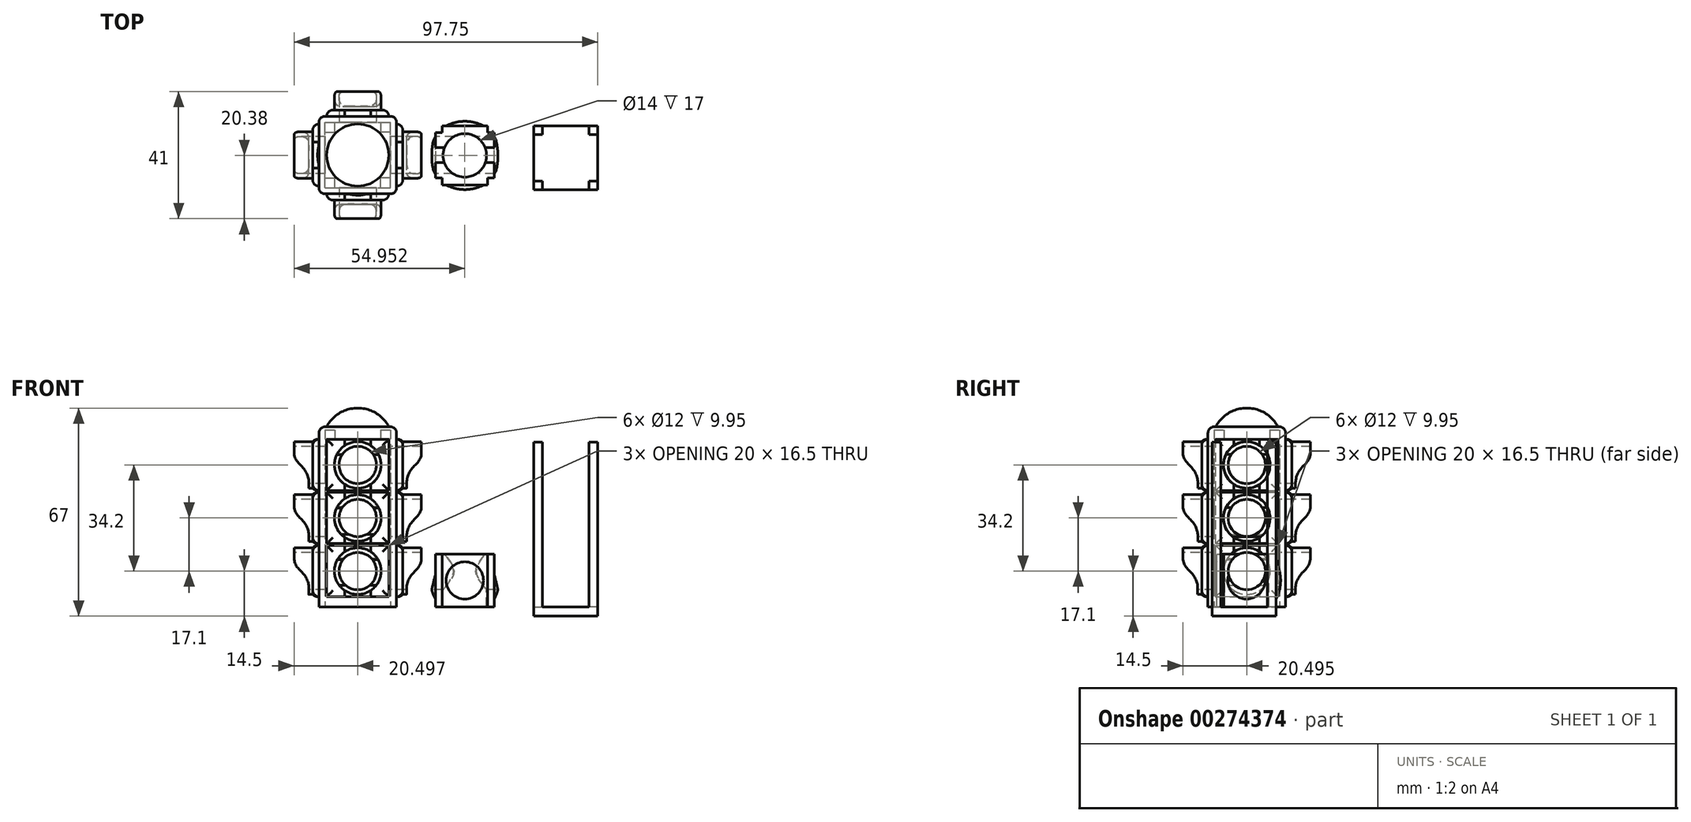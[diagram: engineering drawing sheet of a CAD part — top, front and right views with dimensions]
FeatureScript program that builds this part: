
annotation { "Feature Type Name" : "Feature", "Feature Type Description" : "" }
export const myFeature = defineFeature(function(context is Context, id is Id, definition is map)
    precondition{}
    {
        {
            var Q0;
            Q0=qCreatedBy(makeId("Front.planeOp"),FACE);
            var sketch = newSketch(context, id + "F0", { "sketchPlane" : qUnion([Q0])});
            skLineSegment(sketch, "E0.bottom", {"start": v(-22.57, 17) * mm, "end": v(-3.57, 17) * mm});
            skLineSegment(sketch, "E0.top", {"start": v(-22.57, 0) * mm, "end": v(-3.57, 0) * mm});
            skLineSegment(sketch, "E0.left", {"start": v(-22.57, 17) * mm, "end": v(-22.57, 0) * mm});
            skLineSegment(sketch, "E0.right", {"start": v(-3.57, 17) * mm, "end": v(-3.57, 0) * mm});
            skSolve(sketch);
        }
        {
            var Q0;
            Q0=makeQuery(id+"F0.imprint","IMPRINT",FACE,{"disambiguationData":[TD([[makeQuery(id+"F0.imprint","IMPRINT",EDGE,{"derivedFrom":sQuery(id+"F0.wireOp",EDGE,"E0.bottom")}),-1.0]])]});
            extrude(context, id + "F1", {"entities" : qUnion([Q0]), "depth" : 19 * mm});
        }
        {
            var Q0;
            Q0=makeQuery(id+"F1.opExtrude","CAP_FACE",FACE,{"disambiguationData":[OSD([sQuery(id+"F0.wireOp",EDGE,"E0.bottom"),sQuery(id+"F0.wireOp",EDGE,"E0.top"),sQuery(id+"F0.wireOp",EDGE,"E0.left"),sQuery(id+"F0.wireOp",EDGE,"E0.right")])],"isStart":false});
            var sketch = newSketch(context, id + "F2", { "sketchPlane" : qUnion([Q0])});
            skCircle(sketch, "E1", {"center": v(-13.07, 8.5) * mm, "radius": 6 * mm});
            skPoint(sketch, "E1.centerSnap0", {"position": v(-22.57, 8.5) * mm});
            skSolve(sketch);
        }
        {
            var Q0;
            Q0=makeQuery(id+"F2.imprint","IMPRINT",FACE,{"disambiguationData":[TD([[makeQuery(id+"F2.imprint","IMPRINT",EDGE,{"derivedFrom":sQuery(id+"F2.wireOp",EDGE,"E1")}),1.0]])]});
            extrude(context, id + "F3", {"entities" : qUnion([Q0]), "operationType" : NewBodyOperationType.ADD, "depth" : 1.5 * mm});
        }
        {
            var Q0;
            Q0=makeQuery(id+"F1.opExtrude","SWEPT_FACE",FACE,{"disambiguationData":[OSD([sQuery(id+"F0.wireOp",EDGE,"E0.left")])]});
            var sketch = newSketch(context, id + "F4", { "sketchPlane" : qUnion([Q0])});
            skCircle(sketch, "E2", {"center": v(9.5, 8.5) * mm, "radius": 6 * mm});
            skSolve(sketch);
        }
        {
            var Q0;
            Q0=makeQuery(id+"F4.imprint","IMPRINT",FACE,{"disambiguationData":[TD([[makeQuery(id+"F4.imprint","IMPRINT",EDGE,{"derivedFrom":sQuery(id+"F4.wireOp",EDGE,"E2")}),1.0]])]});
            extrude(context, id + "F5", {"entities" : qUnion([Q0]), "operationType" : NewBodyOperationType.ADD, "depth" : 1.5 * mm});
        }
        {
            var Q0;
            Q0=makeQuery(id+"F1.opExtrude","CAP_FACE",FACE,{"disambiguationData":[OSD([sQuery(id+"F0.wireOp",EDGE,"E0.bottom"),sQuery(id+"F0.wireOp",EDGE,"E0.top"),sQuery(id+"F0.wireOp",EDGE,"E0.left"),sQuery(id+"F0.wireOp",EDGE,"E0.right")])],"isStart":true});
            var sketch = newSketch(context, id + "F6", { "sketchPlane" : qUnion([Q0])});
            skCircle(sketch, "E3", {"center": v(13.07, 8.5) * mm, "radius": 6 * mm});
            skSolve(sketch);
        }
        {
            var Q0;
            Q0=makeQuery(id+"F6.imprint","IMPRINT",FACE,{"disambiguationData":[TD([[makeQuery(id+"F6.imprint","IMPRINT",EDGE,{"derivedFrom":sQuery(id+"F6.wireOp",EDGE,"E3")}),1.0]])]});
            extrude(context, id + "F7", {"entities" : qUnion([Q0]), "operationType" : NewBodyOperationType.ADD, "depth" : 1.5 * mm});
        }
        {
            var Q0;
            Q0=makeQuery(id+"F1.opExtrude","SWEPT_FACE",FACE,{"disambiguationData":[OSD([sQuery(id+"F0.wireOp",EDGE,"E0.right")])]});
            var sketch = newSketch(context, id + "F8", { "sketchPlane" : qUnion([Q0])});
            skCircle(sketch, "E4", {"center": v(-9.5, 8.5) * mm, "radius": 6 * mm});
            skPoint(sketch, "E4.centerSnap0", {"position": v(-19, 8.5) * mm});
            skSolve(sketch);
        }
        {
            var Q0;
            Q0=makeQuery(id+"F8.imprint","IMPRINT",FACE,{"disambiguationData":[TD([[makeQuery(id+"F8.imprint","IMPRINT",EDGE,{"derivedFrom":sQuery(id+"F8.wireOp",EDGE,"E4")}),1.0]])]});
            extrude(context, id + "F9", {"entities" : qUnion([Q0]), "operationType" : NewBodyOperationType.ADD, "depth" : 1.5 * mm});
        }
        {
            var Q0;
            Q0=makeQuery(id+"F3.opExtrude","CAP_EDGE",EDGE,{"disambiguationData":[OSD([sQuery(id+"F2.wireOp",EDGE,"E1")])],"isStart":false});
            var Q1;
            Q1=makeQuery(id+"F5.opExtrude","CAP_EDGE",EDGE,{"disambiguationData":[OSD([sQuery(id+"F4.wireOp",EDGE,"E2")])],"isStart":false});
            var Q2;
            Q2=makeQuery(id+"F7.opExtrude","CAP_EDGE",EDGE,{"disambiguationData":[OSD([sQuery(id+"F6.wireOp",EDGE,"E3")])],"isStart":false});
            var Q3;
            Q3=makeQuery(id+"F9.opExtrude","CAP_EDGE",EDGE,{"disambiguationData":[OSD([sQuery(id+"F8.wireOp",EDGE,"E4")])],"isStart":false});
            fillet(context, id + "F10", {"entities" : qUnion([Q0, Q1, Q2, Q3]), "radius" : 12.7 * mm, "tangentPropagation" : true, "allowEdgeOverflow" : false});
        }
        {
            var Q0;
            Q0=makeQuery(id+"F1.opExtrude","SWEPT_FACE",FACE,{"disambiguationData":[OSD([sQuery(id+"F0.wireOp",EDGE,"E0.bottom")])]});
            var sketch = newSketch(context, id + "F11", { "sketchPlane" : qUnion([Q0])});
            skLineSegment(sketch, "E5.bottom", {"start": v(-22.57, 0) * mm, "end": v(-20.37, 0) * mm});
            skLineSegment(sketch, "E5.top", {"start": v(-22.57, -2.2) * mm, "end": v(-20.37, -2.2) * mm});
            skLineSegment(sketch, "E5.left", {"start": v(-22.57, 0) * mm, "end": v(-22.57, -2.2) * mm});
            skLineSegment(sketch, "E5.right", {"start": v(-20.37, 0) * mm, "end": v(-20.37, -2.2) * mm});
            skLineSegment(sketch, "E6.bottom", {"start": v(-3.57, 0) * mm, "end": v(-5.77, 0) * mm});
            skLineSegment(sketch, "E6.top", {"start": v(-3.57, -2.2) * mm, "end": v(-5.77, -2.2) * mm});
            skLineSegment(sketch, "E6.left", {"start": v(-3.57, 0) * mm, "end": v(-3.57, -2.2) * mm});
            skLineSegment(sketch, "E6.right", {"start": v(-5.77, 0) * mm, "end": v(-5.77, -2.2) * mm});
            skLineSegment(sketch, "E7.bottom", {"start": v(-22.57, -19) * mm, "end": v(-20.37, -19) * mm});
            skLineSegment(sketch, "E7.top", {"start": v(-22.57, -16.8) * mm, "end": v(-20.37, -16.8) * mm});
            skLineSegment(sketch, "E7.left", {"start": v(-22.57, -19) * mm, "end": v(-22.57, -16.8) * mm});
            skLineSegment(sketch, "E7.right", {"start": v(-20.37, -19) * mm, "end": v(-20.37, -16.8) * mm});
            skLineSegment(sketch, "E8.bottom", {"start": v(-3.57, -19) * mm, "end": v(-5.77, -19) * mm});
            skLineSegment(sketch, "E8.top", {"start": v(-3.57, -16.8) * mm, "end": v(-5.77, -16.8) * mm});
            skLineSegment(sketch, "E8.left", {"start": v(-3.57, -19) * mm, "end": v(-3.57, -16.8) * mm});
            skLineSegment(sketch, "E8.right", {"start": v(-5.77, -19) * mm, "end": v(-5.77, -16.8) * mm});
            skSolve(sketch);
        }
        {
            var Q0;
            Q0=makeQuery(id+"F11.imprint","IMPRINT",FACE,{"disambiguationData":[TD([[makeQuery(id+"F11.imprint","IMPRINT",EDGE,{"derivedFrom":sQuery(id+"F11.wireOp",EDGE,"E5.bottom")}),-1.0]])]});
            var Q1;
            Q1=makeQuery(id+"F11.imprint","IMPRINT",FACE,{"disambiguationData":[TD([[makeQuery(id+"F11.imprint","IMPRINT",EDGE,{"derivedFrom":sQuery(id+"F11.wireOp",EDGE,"E6.bottom")}),-1.0]])]});
            var Q2;
            Q2=makeQuery(id+"F11.imprint","IMPRINT",FACE,{"disambiguationData":[TD([[makeQuery(id+"F11.imprint","IMPRINT",EDGE,{"derivedFrom":sQuery(id+"F11.wireOp",EDGE,"E8.bottom")}),1.0]])]});
            var Q3;
            Q3=makeQuery(id+"F11.imprint","IMPRINT",FACE,{"disambiguationData":[TD([[makeQuery(id+"F11.imprint","IMPRINT",EDGE,{"derivedFrom":sQuery(id+"F11.wireOp",EDGE,"E7.bottom")}),1.0]])]});
            extrude(context, id + "F12", {"entities" : qUnion([Q0, Q1, Q2, Q3]), "operationType" : NewBodyOperationType.REMOVE, "endBound" : BoundingType.THROUGH_ALL, "oppositeDirection" : true, "depth" : 25 * mm});
        }
        {
            var Q0;
            Q0=qCreatedBy(makeId("Top.planeOp"),FACE);
            var sketch = newSketch(context, id + "F13", { "sketchPlane" : qUnion([Q0])});
            skLineSegment(sketch, "E9.bottom", {"start": v(9.13, 0) * mm, "end": v(29.73, 0) * mm});
            skLineSegment(sketch, "E9.top", {"start": v(9.13, -20.6) * mm, "end": v(29.73, -20.6) * mm});
            skLineSegment(sketch, "E9.left", {"start": v(9.13, 0) * mm, "end": v(9.13, -20.6) * mm});
            skLineSegment(sketch, "E9.right", {"start": v(29.73, 0) * mm, "end": v(29.73, -20.6) * mm});
            skSolve(sketch);
        }
        {
            var Q0;
            Q0=makeQuery(id+"F13.imprint","IMPRINT",FACE,{"disambiguationData":[TD([[makeQuery(id+"F13.imprint","IMPRINT",EDGE,{"derivedFrom":sQuery(id+"F13.wireOp",EDGE,"E9.bottom")}),-1.0]])]});
            extrude(context, id + "F14", {"entities" : qUnion([Q0]), "oppositeDirection" : true, "depth" : 3 * mm});
        }
        {
            var Q0;
            Q0=makeQuery(id+"F14.opExtrude","CAP_FACE",FACE,{"disambiguationData":[OSD([sQuery(id+"F13.wireOp",EDGE,"E9.bottom"),sQuery(id+"F13.wireOp",EDGE,"E9.top"),sQuery(id+"F13.wireOp",EDGE,"E9.left"),sQuery(id+"F13.wireOp",EDGE,"E9.right")])],"isStart":true});
            var sketch = newSketch(context, id + "F15", { "sketchPlane" : qUnion([Q0])});
            skLineSegment(sketch, "E10.bottom", {"start": v(9.13, 0) * mm, "end": v(11.93, 0) * mm});
            skLineSegment(sketch, "E10.top", {"start": v(9.13, -2.8) * mm, "end": v(11.93, -2.8) * mm});
            skLineSegment(sketch, "E10.left", {"start": v(9.13, 0) * mm, "end": v(9.13, -2.8) * mm});
            skLineSegment(sketch, "E10.right", {"start": v(11.93, 0) * mm, "end": v(11.93, -2.8) * mm});
            skLineSegment(sketch, "E11.bottom", {"start": v(9.13, -20.6) * mm, "end": v(11.93, -20.6) * mm});
            skLineSegment(sketch, "E11.top", {"start": v(9.13, -17.8) * mm, "end": v(11.93, -17.8) * mm});
            skLineSegment(sketch, "E11.left", {"start": v(9.13, -20.6) * mm, "end": v(9.13, -17.8) * mm});
            skLineSegment(sketch, "E11.right", {"start": v(11.93, -20.6) * mm, "end": v(11.93, -17.8) * mm});
            skLineSegment(sketch, "E12.bottom", {"start": v(29.73, 0) * mm, "end": v(26.93, 0) * mm});
            skLineSegment(sketch, "E12.top", {"start": v(29.73, -2.8) * mm, "end": v(26.93, -2.8) * mm});
            skLineSegment(sketch, "E12.left", {"start": v(29.73, 0) * mm, "end": v(29.73, -2.8) * mm});
            skLineSegment(sketch, "E12.right", {"start": v(26.93, 0) * mm, "end": v(26.93, -2.8) * mm});
            skLineSegment(sketch, "E13.bottom", {"start": v(29.73, -20.6) * mm, "end": v(26.93, -20.6) * mm});
            skLineSegment(sketch, "E13.top", {"start": v(29.73, -17.8) * mm, "end": v(26.93, -17.8) * mm});
            skLineSegment(sketch, "E13.left", {"start": v(29.73, -20.6) * mm, "end": v(29.73, -17.8) * mm});
            skLineSegment(sketch, "E13.right", {"start": v(26.93, -20.6) * mm, "end": v(26.93, -17.8) * mm});
            skSolve(sketch);
        }
        {
            var Q0;
            Q0=makeQuery(id+"F15.imprint","IMPRINT",FACE,{"disambiguationData":[TD([[makeQuery(id+"F15.imprint","IMPRINT",EDGE,{"derivedFrom":sQuery(id+"F15.wireOp",EDGE,"E11.bottom")}),1.0]])]});
            var Q1;
            Q1=makeQuery(id+"F15.imprint","IMPRINT",FACE,{"disambiguationData":[TD([[makeQuery(id+"F15.imprint","IMPRINT",EDGE,{"derivedFrom":sQuery(id+"F15.wireOp",EDGE,"E10.bottom")}),-1.0]])]});
            var Q2;
            Q2=makeQuery(id+"F15.imprint","IMPRINT",FACE,{"disambiguationData":[TD([[makeQuery(id+"F15.imprint","IMPRINT",EDGE,{"derivedFrom":sQuery(id+"F15.wireOp",EDGE,"E12.bottom")}),-1.0]])]});
            var Q3;
            Q3=makeQuery(id+"F15.imprint","IMPRINT",FACE,{"disambiguationData":[TD([[makeQuery(id+"F15.imprint","IMPRINT",EDGE,{"derivedFrom":sQuery(id+"F15.wireOp",EDGE,"E13.bottom")}),1.0]])]});
            extrude(context, id + "F16", {"entities" : qUnion([Q0, Q1, Q2, Q3]), "operationType" : NewBodyOperationType.ADD, "depth" : 53 * mm});
        }
        {
            var Q0;
            Q0=qCreatedBy(makeId("Top.planeOp"),FACE);
            var sketch = newSketch(context, id + "F17", { "sketchPlane" : qUnion([Q0])});
            skLineSegment(sketch, "E14.bottom", {"start": v(-60.02, 3.12) * mm, "end": v(-35.02, 3.12) * mm});
            skLineSegment(sketch, "E14.top", {"start": v(-60.02, -21.88) * mm, "end": v(-35.02, -21.88) * mm});
            skLineSegment(sketch, "E14.left", {"start": v(-60.02, 3.12) * mm, "end": v(-60.02, -21.88) * mm});
            skLineSegment(sketch, "E14.right", {"start": v(-35.02, 3.12) * mm, "end": v(-35.02, -21.88) * mm});
            skSolve(sketch);
        }
        {
            var Q0;
            Q0=makeQuery(id+"F17.imprint","IMPRINT",FACE,{"disambiguationData":[TD([[makeQuery(id+"F17.imprint","IMPRINT",EDGE,{"derivedFrom":sQuery(id+"F17.wireOp",EDGE,"E14.bottom")}),-1.0]])]});
            extrude(context, id + "F18", {"entities" : qUnion([Q0]), "depth" : 58 * mm});
        }
        {
            var Q0;
            Q0=makeQuery(id+"F18.opExtrude","CAP_FACE",FACE,{"disambiguationData":[OSD([sQuery(id+"F17.wireOp",EDGE,"E14.bottom"),sQuery(id+"F17.wireOp",EDGE,"E14.top"),sQuery(id+"F17.wireOp",EDGE,"E14.left"),sQuery(id+"F17.wireOp",EDGE,"E14.right")])],"isStart":true});
            var sketch = newSketch(context, id + "F19", { "sketchPlane" : qUnion([Q0])});
            skLineSegment(sketch, "E15.bottom", {"start": v(-58.07, 19.93) * mm, "end": v(-36.97, 19.93) * mm});
            skLineSegment(sketch, "E15.top", {"start": v(-58.07, -1.17) * mm, "end": v(-36.97, -1.17) * mm});
            skLineSegment(sketch, "E15.left", {"start": v(-58.07, 19.93) * mm, "end": v(-58.07, -1.17) * mm});
            skLineSegment(sketch, "E15.right", {"start": v(-36.97, 19.93) * mm, "end": v(-36.97, -1.17) * mm});
            skPoint(sketch, "E15.middle", {"position": v(-47.52, 9.38) * mm});
            skSolve(sketch);
        }
        {
            var Q0;
            Q0=makeQuery(id+"F18.opExtrude","SWEPT_FACE",FACE,{"disambiguationData":[OSD([sQuery(id+"F17.wireOp",EDGE,"E14.top")])]});
            var sketch = newSketch(context, id + "F20", { "sketchPlane" : qUnion([Q0])});
            skCircle(sketch, "E16", {"center": v(-47.52, 11.5) * mm, "radius": 6 * mm});
            skCircle(sketch, "E17.0.1.0", {"center": v(-47.52, 28.6) * mm, "radius": 6 * mm});
            skCircle(sketch, "E17.0.2.0", {"center": v(-47.52, 45.7) * mm, "radius": 6 * mm});
            skLineSegment(sketch, "E17.direction1", {"start": v(-47.52, 11.5) * mm, "end": v(-22.52, 11.5) * mm, "construction": true});
            skLineSegment(sketch, "E17.direction2", {"start": v(-47.52, 11.5) * mm, "end": v(-47.52, 28.6) * mm, "construction": true});
            skCircle(sketch, "E18", {"center": v(-47.52, 11.5) * mm, "radius": 7.5 * mm});
            skCircle(sketch, "E19.0.1.0", {"center": v(-47.52, 28.6) * mm, "radius": 7.5 * mm});
            skCircle(sketch, "E19.0.2.0", {"center": v(-47.52, 45.7) * mm, "radius": 7.5 * mm});
            skLineSegment(sketch, "E20.bottom", {"start": v(-37.52, 19.75) * mm, "end": v(-57.52, 19.75) * mm});
            skLineSegment(sketch, "E20.top", {"start": v(-37.52, 3.25) * mm, "end": v(-57.52, 3.25) * mm});
            skLineSegment(sketch, "E20.left", {"start": v(-37.52, 19.75) * mm, "end": v(-37.52, 3.25) * mm});
            skLineSegment(sketch, "E20.right", {"start": v(-57.52, 19.75) * mm, "end": v(-57.52, 3.25) * mm});
            skLineSegment(sketch, "E21.0.1.0", {"start": v(-37.52, 36.85) * mm, "end": v(-57.52, 36.85) * mm});
            skLineSegment(sketch, "E21.0.1.1", {"start": v(-37.52, 36.85) * mm, "end": v(-37.52, 20.35) * mm});
            skLineSegment(sketch, "E21.0.1.2", {"start": v(-37.52, 20.35) * mm, "end": v(-57.52, 20.35) * mm});
            skLineSegment(sketch, "E21.0.1.3", {"start": v(-57.52, 36.85) * mm, "end": v(-57.52, 20.35) * mm});
            skLineSegment(sketch, "E21.0.2.0", {"start": v(-37.52, 53.95) * mm, "end": v(-57.52, 53.95) * mm});
            skLineSegment(sketch, "E21.0.2.1", {"start": v(-37.52, 53.95) * mm, "end": v(-37.52, 37.45) * mm});
            skLineSegment(sketch, "E21.0.2.2", {"start": v(-37.52, 37.45) * mm, "end": v(-57.52, 37.45) * mm});
            skLineSegment(sketch, "E21.0.2.3", {"start": v(-57.52, 53.95) * mm, "end": v(-57.52, 37.45) * mm});
            skLineSegment(sketch, "E21.direction1", {"start": v(-57.52, 3.25) * mm, "end": v(-32.52, 3.25) * mm, "construction": true});
            skLineSegment(sketch, "E21.direction2", {"start": v(-57.52, 3.25) * mm, "end": v(-57.52, 20.35) * mm, "construction": true});
            skSolve(sketch);
        }
        {
            var Q0;
            Q0=makeQuery(id+"F20.imprint","IMPRINT",FACE,{"disambiguationData":[TD([[makeQuery(id+"F20.imprint","IMPRINT",EDGE,{"derivedFrom":sQuery(id+"F20.wireOp",EDGE,"E16")}),1.0]])]});
            var Q1;
            Q1=makeQuery(id+"F20.imprint","IMPRINT",FACE,{"disambiguationData":[TD([[makeQuery(id+"F20.imprint","IMPRINT",EDGE,{"derivedFrom":sQuery(id+"F20.wireOp",EDGE,"E17.0.1.0")}),1.0]])]});
            var Q2;
            Q2=makeQuery(id+"F20.imprint","IMPRINT",FACE,{"disambiguationData":[TD([[makeQuery(id+"F20.imprint","IMPRINT",EDGE,{"derivedFrom":sQuery(id+"F20.wireOp",EDGE,"E17.0.2.0")}),1.0]])]});
            extrude(context, id + "F21", {"entities" : qUnion([Q0, Q1, Q2]), "operationType" : NewBodyOperationType.REMOVE, "flatOperationType" : FlatOperationType.REMOVE, "endBound" : BoundingType.THROUGH_ALL, "oppositeDirection" : true, "offsetDistance" : 25 * mm, "depth" : 25 * mm, "domain" : OperationDomain.MODEL});
        }
        {
            var Q0;
            Q0=makeQuery(id+"F20.imprint","IMPRINT",FACE,{"disambiguationData":[TD([[makeQuery(id+"F20.imprint","IMPRINT",EDGE,{"derivedFrom":sQuery(id+"F20.wireOp",EDGE,"E17.0.2.0")}),-1.0]])]});
            var Q1;
            Q1=makeQuery(id+"F20.imprint","IMPRINT",FACE,{"disambiguationData":[TD([[makeQuery(id+"F20.imprint","IMPRINT",EDGE,{"derivedFrom":sQuery(id+"F20.wireOp",EDGE,"E17.0.1.0")}),-1.0]])]});
            var Q2;
            Q2=makeQuery(id+"F20.imprint","IMPRINT",FACE,{"disambiguationData":[TD([[makeQuery(id+"F20.imprint","IMPRINT",EDGE,{"derivedFrom":sQuery(id+"F20.wireOp",EDGE,"E16")}),-1.0]])]});
            extrude(context, id + "F22", {"entities" : qUnion([Q0, Q1, Q2]), "operationType" : NewBodyOperationType.ADD, "flatOperationType" : FlatOperationType.REMOVE, "offsetDistance" : 25 * mm, "depth" : 8 * mm, "hasSecondDirection" : true, "secondDirectionOppositeDirection" : true, "secondDirectionDepth" : 33 * mm, "domain" : OperationDomain.MODEL});
        }
        {
            var Q0;
            Q0=makeQuery(id+"F20.imprint","IMPRINT",FACE,{"disambiguationData":[TD([[makeQuery(id+"F20.imprint","IMPRINT",EDGE,{"derivedFrom":sQuery(id+"F20.wireOp",EDGE,"E19.0.2.0")}),-1.0]])]});
            var Q1;
            Q1=makeQuery(id+"F20.imprint","IMPRINT",FACE,{"disambiguationData":[TD([[makeQuery(id+"F20.imprint","IMPRINT",EDGE,{"derivedFrom":sQuery(id+"F20.wireOp",EDGE,"E19.0.1.0")}),-1.0]])]});
            var Q2;
            Q2=makeQuery(id+"F20.imprint","IMPRINT",FACE,{"disambiguationData":[TD([[makeQuery(id+"F20.imprint","IMPRINT",EDGE,{"derivedFrom":sQuery(id+"F20.wireOp",EDGE,"E18")}),-1.0]])]});
            extrude(context, id + "F23", {"entities" : qUnion([Q0, Q1, Q2]), "operationType" : NewBodyOperationType.ADD, "flatOperationType" : FlatOperationType.REMOVE, "offsetDistance" : 25 * mm, "depth" : 2 * mm, "hasSecondDirection" : true, "secondDirectionOppositeDirection" : true, "secondDirectionDepth" : 27 * mm, "domain" : OperationDomain.MODEL});
        }
        {
            var Q0;
            Q0=makeQuery(id+"F18.opExtrude","SWEPT_FACE",FACE,{"disambiguationData":[OSD([sQuery(id+"F17.wireOp",EDGE,"E14.left")])]});
            var sketch = newSketch(context, id + "F24", { "sketchPlane" : qUnion([Q0])});
            skCircle(sketch, "E22", {"center": v(9.38, 11.5) * mm, "radius": 6 * mm});
            skCircle(sketch, "E23.0.1.0", {"center": v(9.38, 28.6) * mm, "radius": 6 * mm});
            skCircle(sketch, "E23.0.2.0", {"center": v(9.38, 45.7) * mm, "radius": 6 * mm});
            skLineSegment(sketch, "E23.direction1", {"start": v(9.38, 11.5) * mm, "end": v(34.38, 11.5) * mm, "construction": true});
            skLineSegment(sketch, "E23.direction2", {"start": v(9.38, 11.5) * mm, "end": v(9.38, 28.6) * mm, "construction": true});
            skCircle(sketch, "E24", {"center": v(9.38, 11.5) * mm, "radius": 7.5 * mm});
            skCircle(sketch, "E25.0.1.0", {"center": v(9.38, 28.6) * mm, "radius": 7.5 * mm});
            skCircle(sketch, "E25.0.2.0", {"center": v(9.38, 45.7) * mm, "radius": 7.5 * mm});
            skLineSegment(sketch, "E26.bottom", {"start": v(19.38, 3.25) * mm, "end": v(-0.62, 3.25) * mm});
            skLineSegment(sketch, "E26.top", {"start": v(19.38, 19.75) * mm, "end": v(-0.62, 19.75) * mm});
            skLineSegment(sketch, "E26.left", {"start": v(19.38, 3.25) * mm, "end": v(19.38, 19.75) * mm});
            skLineSegment(sketch, "E26.right", {"start": v(-0.62, 3.25) * mm, "end": v(-0.62, 19.75) * mm});
            skLineSegment(sketch, "E27.0.1.0", {"start": v(19.38, 36.85) * mm, "end": v(-0.62, 36.85) * mm});
            skLineSegment(sketch, "E27.0.1.1", {"start": v(19.38, 20.35) * mm, "end": v(19.38, 36.85) * mm});
            skLineSegment(sketch, "E27.0.1.2", {"start": v(19.38, 20.35) * mm, "end": v(-0.62, 20.35) * mm});
            skLineSegment(sketch, "E27.0.1.3", {"start": v(-0.62, 20.35) * mm, "end": v(-0.62, 36.85) * mm});
            skLineSegment(sketch, "E27.0.2.0", {"start": v(19.38, 53.95) * mm, "end": v(-0.62, 53.95) * mm});
            skLineSegment(sketch, "E27.0.2.1", {"start": v(19.38, 37.45) * mm, "end": v(19.38, 53.95) * mm});
            skLineSegment(sketch, "E27.0.2.2", {"start": v(19.38, 37.45) * mm, "end": v(-0.62, 37.45) * mm});
            skLineSegment(sketch, "E27.0.2.3", {"start": v(-0.62, 37.45) * mm, "end": v(-0.62, 53.95) * mm});
            skLineSegment(sketch, "E27.direction1", {"start": v(-0.62, 3.25) * mm, "end": v(24.38, 3.25) * mm, "construction": true});
            skLineSegment(sketch, "E27.direction2", {"start": v(-0.62, 3.25) * mm, "end": v(-0.62, 20.35) * mm, "construction": true});
            skSolve(sketch);
        }
        {
            var Q0;
            Q0=makeQuery(id+"F24.imprint","IMPRINT",FACE,{"disambiguationData":[TD([[makeQuery(id+"F24.imprint","IMPRINT",EDGE,{"derivedFrom":sQuery(id+"F24.wireOp",EDGE,"E23.0.2.0")}),1.0]])]});
            var Q1;
            Q1=makeQuery(id+"F24.imprint","IMPRINT",FACE,{"disambiguationData":[TD([[makeQuery(id+"F24.imprint","IMPRINT",EDGE,{"derivedFrom":sQuery(id+"F24.wireOp",EDGE,"E23.0.1.0")}),1.0]])]});
            var Q2;
            Q2=makeQuery(id+"F24.imprint","IMPRINT",FACE,{"disambiguationData":[TD([[makeQuery(id+"F24.imprint","IMPRINT",EDGE,{"derivedFrom":sQuery(id+"F24.wireOp",EDGE,"E22")}),1.0]])]});
            extrude(context, id + "F25", {"entities" : qUnion([Q0, Q1, Q2]), "operationType" : NewBodyOperationType.REMOVE, "endBound" : BoundingType.THROUGH_ALL, "oppositeDirection" : true, "depth" : 25 * mm});
        }
        {
            var Q0;
            Q0=makeQuery(id+"F24.imprint","IMPRINT",FACE,{"disambiguationData":[TD([[makeQuery(id+"F24.imprint","IMPRINT",EDGE,{"derivedFrom":sQuery(id+"F24.wireOp",EDGE,"E22")}),-1.0]])]});
            var Q1;
            Q1=makeQuery(id+"F24.imprint","IMPRINT",FACE,{"disambiguationData":[TD([[makeQuery(id+"F24.imprint","IMPRINT",EDGE,{"derivedFrom":sQuery(id+"F24.wireOp",EDGE,"E23.0.1.0")}),-1.0]])]});
            var Q2;
            Q2=makeQuery(id+"F24.imprint","IMPRINT",FACE,{"disambiguationData":[TD([[makeQuery(id+"F24.imprint","IMPRINT",EDGE,{"derivedFrom":sQuery(id+"F24.wireOp",EDGE,"E23.0.2.0")}),-1.0]])]});
            extrude(context, id + "F26", {"entities" : qUnion([Q0, Q1, Q2]), "operationType" : NewBodyOperationType.ADD, "depth" : 8 * mm, "hasSecondDirection" : true, "secondDirectionOppositeDirection" : true, "secondDirectionDepth" : 33 * mm});
        }
        {
            var Q0;
            Q0=makeQuery(id+"F24.imprint","IMPRINT",FACE,{"disambiguationData":[TD([[makeQuery(id+"F24.imprint","IMPRINT",EDGE,{"derivedFrom":sQuery(id+"F24.wireOp",EDGE,"E24")}),-1.0]])]});
            var Q1;
            Q1=makeQuery(id+"F24.imprint","IMPRINT",FACE,{"disambiguationData":[TD([[makeQuery(id+"F24.imprint","IMPRINT",EDGE,{"derivedFrom":sQuery(id+"F24.wireOp",EDGE,"E25.0.1.0")}),-1.0]])]});
            var Q2;
            Q2=makeQuery(id+"F24.imprint","IMPRINT",FACE,{"disambiguationData":[TD([[makeQuery(id+"F24.imprint","IMPRINT",EDGE,{"derivedFrom":sQuery(id+"F24.wireOp",EDGE,"E25.0.2.0")}),-1.0]])]});
            extrude(context, id + "F27", {"entities" : qUnion([Q0, Q1, Q2]), "operationType" : NewBodyOperationType.ADD, "depth" : 2 * mm, "hasSecondDirection" : true, "secondDirectionOppositeDirection" : true, "secondDirectionDepth" : 27 * mm});
        }
        {
            var Q0;
            Q0=makeQuery(id+"F19.imprint","IMPRINT",FACE,{"disambiguationData":[TD([[makeQuery(id+"F19.imprint","IMPRINT",EDGE,{"derivedFrom":sQuery(id+"F19.wireOp",EDGE,"E15.bottom")}),-1.0]])]});
            extrude(context, id + "F28", {"entities" : qUnion([Q0]), "operationType" : NewBodyOperationType.REMOVE, "oppositeDirection" : true, "depth" : 54 * mm});
        }
        {
            var Q0;
            Q0=makeQuery(id+"F28.boolean.opBoolean","COPY",FACE,{"derivedFrom":makeQuery(id+"F28.opExtrude","CAP_FACE",FACE,{"disambiguationData":[OSD([sQuery(id+"F19.wireOp",EDGE,"E15.bottom"),sQuery(id+"F19.wireOp",EDGE,"E15.top"),sQuery(id+"F19.wireOp",EDGE,"E15.left"),sQuery(id+"F19.wireOp",EDGE,"E15.right")])],"isStart":false})});
            var sketch = newSketch(context, id + "F29", { "sketchPlane" : qUnion([Q0])});
            skLineSegment(sketch, "E28.bottom", {"start": v(-58.07, 19.93) * mm, "end": v(-54.87, 19.93) * mm});
            skLineSegment(sketch, "E28.top", {"start": v(-58.07, 16.73) * mm, "end": v(-54.87, 16.73) * mm});
            skLineSegment(sketch, "E28.left", {"start": v(-58.07, 19.93) * mm, "end": v(-58.07, 16.73) * mm});
            skLineSegment(sketch, "E28.right", {"start": v(-54.87, 19.93) * mm, "end": v(-54.87, 16.73) * mm});
            skLineSegment(sketch, "E29.bottom", {"start": v(-58.07, 2.03) * mm, "end": v(-54.87, 2.03) * mm});
            skLineSegment(sketch, "E29.top", {"start": v(-58.07, -1.17) * mm, "end": v(-54.87, -1.17) * mm});
            skLineSegment(sketch, "E29.left", {"start": v(-58.07, 2.03) * mm, "end": v(-58.07, -1.17) * mm});
            skLineSegment(sketch, "E29.right", {"start": v(-54.87, 2.03) * mm, "end": v(-54.87, -1.17) * mm});
            skLineSegment(sketch, "E30.bottom", {"start": v(-36.97, -1.17) * mm, "end": v(-40.17, -1.17) * mm});
            skLineSegment(sketch, "E30.top", {"start": v(-36.97, 2.03) * mm, "end": v(-40.17, 2.03) * mm});
            skLineSegment(sketch, "E30.left", {"start": v(-36.97, -1.17) * mm, "end": v(-36.97, 2.03) * mm});
            skLineSegment(sketch, "E30.right", {"start": v(-40.17, -1.17) * mm, "end": v(-40.17, 2.03) * mm});
            skLineSegment(sketch, "E31.bottom", {"start": v(-36.97, 19.93) * mm, "end": v(-40.17, 19.93) * mm});
            skLineSegment(sketch, "E31.top", {"start": v(-36.97, 16.73) * mm, "end": v(-40.17, 16.73) * mm});
            skLineSegment(sketch, "E31.left", {"start": v(-36.97, 19.93) * mm, "end": v(-36.97, 16.73) * mm});
            skLineSegment(sketch, "E31.right", {"start": v(-40.17, 19.93) * mm, "end": v(-40.17, 16.73) * mm});
            skSolve(sketch);
        }
        {
            var Q0;
            Q0=makeQuery(id+"F29.imprint","IMPRINT",FACE,{"disambiguationData":[TD([[makeQuery(id+"F29.imprint","IMPRINT",EDGE,{"derivedFrom":sQuery(id+"F29.wireOp",EDGE,"E28.bottom")}),-1.0]])]});
            var Q1;
            Q1=makeQuery(id+"F29.imprint","IMPRINT",FACE,{"disambiguationData":[TD([[makeQuery(id+"F29.imprint","IMPRINT",EDGE,{"derivedFrom":sQuery(id+"F29.wireOp",EDGE,"E31.bottom")}),-1.0]])]});
            var Q2;
            Q2=makeQuery(id+"F29.imprint","IMPRINT",FACE,{"disambiguationData":[TD([[makeQuery(id+"F29.imprint","IMPRINT",EDGE,{"derivedFrom":sQuery(id+"F29.wireOp",EDGE,"E30.bottom")}),1.0]])]});
            var Q3;
            Q3=makeQuery(id+"F29.imprint","IMPRINT",FACE,{"disambiguationData":[TD([[makeQuery(id+"F29.imprint","IMPRINT",EDGE,{"derivedFrom":sQuery(id+"F29.wireOp",EDGE,"E29.bottom")}),-1.0]])]});
            extrude(context, id + "F30", {"entities" : qUnion([Q0, Q1, Q2, Q3]), "operationType" : NewBodyOperationType.REMOVE, "oppositeDirection" : true, "depth" : 3 * mm});
        }
        {
            var Q0;
            Q0=makeQuery(id+"F18.opExtrude","CAP_FACE",FACE,{"disambiguationData":[OSD([sQuery(id+"F17.wireOp",EDGE,"E14.bottom"),sQuery(id+"F17.wireOp",EDGE,"E14.top"),sQuery(id+"F17.wireOp",EDGE,"E14.left"),sQuery(id+"F17.wireOp",EDGE,"E14.right")])],"isStart":false});
            var sketch = newSketch(context, id + "F31", { "sketchPlane" : qUnion([Q0])});
            skCircle(sketch, "E32", {"center": v(-47.52, -9.38) * mm, "radius": 10 * mm});
            skPoint(sketch, "E32.centerSnap0", {"position": v(-47.52, -19.82) * mm});
            skSolve(sketch);
        }
        {
            var Q0;
            Q0=makeQuery(id+"F31.imprint","IMPRINT",FACE,{"disambiguationData":[TD([[makeQuery(id+"F31.imprint","IMPRINT",EDGE,{"derivedFrom":sQuery(id+"F31.wireOp",EDGE,"E32")}),1.0]])]});
            extrude(context, id + "F32", {"entities" : qUnion([Q0]), "operationType" : NewBodyOperationType.ADD, "depth" : 6 * mm});
        }
        {
            var Q0;
            Q0=makeQuery(id+"F23.opExtrude","CAP_EDGE",EDGE,{"disambiguationData":[OSD([sQuery(id+"F20.wireOp",EDGE,"E21.0.2.0")])],"isStart":false});
            var Q1;
            Q1=makeQuery(id+"F23.opExtrude","CAP_EDGE",EDGE,{"disambiguationData":[OSD([sQuery(id+"F20.wireOp",EDGE,"E21.0.2.1")])],"isStart":false});
            var Q2;
            Q2=makeQuery(id+"F23.opExtrude","CAP_EDGE",EDGE,{"disambiguationData":[OSD([sQuery(id+"F20.wireOp",EDGE,"E21.0.2.2")])],"isStart":false});
            var Q3;
            Q3=makeQuery(id+"F23.opExtrude","CAP_EDGE",EDGE,{"disambiguationData":[OSD([sQuery(id+"F20.wireOp",EDGE,"E21.0.2.3")])],"isStart":false});
            var Q4;
            Q4=makeQuery(id+"F23.opExtrude","CAP_EDGE",EDGE,{"disambiguationData":[OSD([sQuery(id+"F20.wireOp",EDGE,"E21.0.1.3")])],"isStart":false});
            var Q5;
            Q5=makeQuery(id+"F23.opExtrude","CAP_EDGE",EDGE,{"disambiguationData":[OSD([sQuery(id+"F20.wireOp",EDGE,"E21.0.1.2")])],"isStart":false});
            var Q6;
            Q6=makeQuery(id+"F23.opExtrude","CAP_EDGE",EDGE,{"disambiguationData":[OSD([sQuery(id+"F20.wireOp",EDGE,"E21.0.1.1")])],"isStart":false});
            var Q7;
            Q7=makeQuery(id+"F23.opExtrude","CAP_EDGE",EDGE,{"disambiguationData":[OSD([sQuery(id+"F20.wireOp",EDGE,"E21.0.1.0")])],"isStart":false});
            var Q8;
            Q8=makeQuery(id+"F23.opExtrude","CAP_EDGE",EDGE,{"disambiguationData":[OSD([sQuery(id+"F20.wireOp",EDGE,"E20.bottom")])],"isStart":false});
            var Q9;
            Q9=makeQuery(id+"F23.opExtrude","CAP_EDGE",EDGE,{"disambiguationData":[OSD([sQuery(id+"F20.wireOp",EDGE,"E20.left")])],"isStart":false});
            var Q10;
            Q10=makeQuery(id+"F23.opExtrude","CAP_EDGE",EDGE,{"disambiguationData":[OSD([sQuery(id+"F20.wireOp",EDGE,"E20.top")])],"isStart":false});
            var Q11;
            Q11=makeQuery(id+"F23.opExtrude","CAP_EDGE",EDGE,{"disambiguationData":[OSD([sQuery(id+"F20.wireOp",EDGE,"E20.right")])],"isStart":false});
            var Q12;
            Q12=makeQuery(id+"F23.opExtrude","CAP_EDGE",EDGE,{"disambiguationData":[OSD([sQuery(id+"F20.wireOp",EDGE,"E21.0.2.0")])],"isStart":true});
            var Q13;
            Q13=makeQuery(id+"F23.opExtrude","CAP_EDGE",EDGE,{"disambiguationData":[OSD([sQuery(id+"F20.wireOp",EDGE,"E21.0.2.3")])],"isStart":true});
            var Q14;
            Q14=makeQuery(id+"F23.opExtrude","CAP_EDGE",EDGE,{"disambiguationData":[OSD([sQuery(id+"F20.wireOp",EDGE,"E21.0.2.1")])],"isStart":true});
            var Q15;
            Q15=makeQuery(id+"F23.opExtrude","CAP_EDGE",EDGE,{"disambiguationData":[OSD([sQuery(id+"F20.wireOp",EDGE,"E21.0.2.2")])],"isStart":true});
            var Q16;
            Q16=makeQuery(id+"F23.opExtrude","CAP_EDGE",EDGE,{"disambiguationData":[OSD([sQuery(id+"F20.wireOp",EDGE,"E21.0.1.0")])],"isStart":true});
            var Q17;
            Q17=makeQuery(id+"F23.opExtrude","CAP_EDGE",EDGE,{"disambiguationData":[OSD([sQuery(id+"F20.wireOp",EDGE,"E21.0.1.1")])],"isStart":true});
            var Q18;
            Q18=makeQuery(id+"F23.opExtrude","CAP_EDGE",EDGE,{"disambiguationData":[OSD([sQuery(id+"F20.wireOp",EDGE,"E21.0.1.3")])],"isStart":true});
            var Q19;
            Q19=makeQuery(id+"F23.opExtrude","CAP_EDGE",EDGE,{"disambiguationData":[OSD([sQuery(id+"F20.wireOp",EDGE,"E21.0.1.2")])],"isStart":true});
            var Q20;
            Q20=makeQuery(id+"F23.opExtrude","CAP_EDGE",EDGE,{"disambiguationData":[OSD([sQuery(id+"F20.wireOp",EDGE,"E20.left")])],"isStart":true});
            var Q21;
            Q21=makeQuery(id+"F23.opExtrude","CAP_EDGE",EDGE,{"disambiguationData":[OSD([sQuery(id+"F20.wireOp",EDGE,"E20.bottom")])],"isStart":true});
            var Q22;
            Q22=makeQuery(id+"F23.opExtrude","CAP_EDGE",EDGE,{"disambiguationData":[OSD([sQuery(id+"F20.wireOp",EDGE,"E20.right")])],"isStart":true});
            var Q23;
            Q23=makeQuery(id+"F23.opExtrude","CAP_EDGE",EDGE,{"disambiguationData":[OSD([sQuery(id+"F20.wireOp",EDGE,"E20.top")])],"isStart":true});
            var Q24;
            Q24=makeQuery(id+"F18.opExtrude","SWEPT_EDGE",EDGE,{"disambiguationData":[OSD([sQuery(id+"F17.wireOp",EDGE,"E14.bottom"),sQuery(id+"F17.wireOp",EDGE,"E14.left")])]});
            var Q25;
            Q25=makeQuery(id+"F18.opExtrude","CAP_EDGE",EDGE,{"disambiguationData":[OSD([sQuery(id+"F17.wireOp",EDGE,"E14.left")])],"isStart":false});
            var Q26;
            Q26=makeQuery(id+"F18.opExtrude","CAP_EDGE",EDGE,{"disambiguationData":[OSD([sQuery(id+"F17.wireOp",EDGE,"E14.bottom")])],"isStart":false});
            var Q27;
            Q27=makeQuery(id+"F18.opExtrude","CAP_EDGE",EDGE,{"disambiguationData":[OSD([sQuery(id+"F17.wireOp",EDGE,"E14.right")])],"isStart":false});
            var Q28;
            Q28=makeQuery(id+"F18.opExtrude","CAP_EDGE",EDGE,{"disambiguationData":[OSD([sQuery(id+"F17.wireOp",EDGE,"E14.top")])],"isStart":false});
            var Q29;
            Q29=makeQuery(id+"F18.opExtrude","SWEPT_EDGE",EDGE,{"disambiguationData":[OSD([sQuery(id+"F17.wireOp",EDGE,"E14.top"),sQuery(id+"F17.wireOp",EDGE,"E14.left")])]});
            var Q30;
            Q30=makeQuery(id+"F18.opExtrude","SWEPT_EDGE",EDGE,{"disambiguationData":[OSD([sQuery(id+"F17.wireOp",EDGE,"E14.top"),sQuery(id+"F17.wireOp",EDGE,"E14.right")])]});
            var Q31;
            Q31=makeQuery(id+"F18.opExtrude","SWEPT_EDGE",EDGE,{"disambiguationData":[OSD([sQuery(id+"F17.wireOp",EDGE,"E14.bottom"),sQuery(id+"F17.wireOp",EDGE,"E14.right")])]});
            var Q32;
            Q32=makeQuery(id+"F27.opExtrude","CAP_EDGE",EDGE,{"disambiguationData":[OSD([sQuery(id+"F24.wireOp",EDGE,"E27.0.2.0")])],"isStart":false});
            var Q33;
            Q33=makeQuery(id+"F27.opExtrude","CAP_EDGE",EDGE,{"disambiguationData":[OSD([sQuery(id+"F24.wireOp",EDGE,"E27.0.2.1")])],"isStart":false});
            var Q34;
            Q34=makeQuery(id+"F27.opExtrude","CAP_EDGE",EDGE,{"disambiguationData":[OSD([sQuery(id+"F24.wireOp",EDGE,"E27.0.2.2")])],"isStart":false});
            var Q35;
            Q35=makeQuery(id+"F27.opExtrude","CAP_EDGE",EDGE,{"disambiguationData":[OSD([sQuery(id+"F24.wireOp",EDGE,"E27.0.2.3")])],"isStart":false});
            var Q36;
            Q36=makeQuery(id+"F27.opExtrude","CAP_EDGE",EDGE,{"disambiguationData":[OSD([sQuery(id+"F24.wireOp",EDGE,"E27.0.1.3")])],"isStart":false});
            var Q37;
            Q37=makeQuery(id+"F27.opExtrude","CAP_EDGE",EDGE,{"disambiguationData":[OSD([sQuery(id+"F24.wireOp",EDGE,"E27.0.1.0")])],"isStart":false});
            var Q38;
            Q38=makeQuery(id+"F27.opExtrude","CAP_EDGE",EDGE,{"disambiguationData":[OSD([sQuery(id+"F24.wireOp",EDGE,"E27.0.1.1")])],"isStart":false});
            var Q39;
            Q39=makeQuery(id+"F27.opExtrude","CAP_EDGE",EDGE,{"disambiguationData":[OSD([sQuery(id+"F24.wireOp",EDGE,"E27.0.1.2")])],"isStart":false});
            var Q40;
            Q40=makeQuery(id+"F27.opExtrude","CAP_EDGE",EDGE,{"disambiguationData":[OSD([sQuery(id+"F24.wireOp",EDGE,"E26.top")])],"isStart":false});
            var Q41;
            Q41=makeQuery(id+"F27.opExtrude","CAP_EDGE",EDGE,{"disambiguationData":[OSD([sQuery(id+"F24.wireOp",EDGE,"E26.right")])],"isStart":false});
            var Q42;
            Q42=makeQuery(id+"F27.opExtrude","CAP_EDGE",EDGE,{"disambiguationData":[OSD([sQuery(id+"F24.wireOp",EDGE,"E26.bottom")])],"isStart":false});
            var Q43;
            Q43=makeQuery(id+"F27.opExtrude","CAP_EDGE",EDGE,{"disambiguationData":[OSD([sQuery(id+"F24.wireOp",EDGE,"E26.left")])],"isStart":false});
            var Q44;
            Q44=makeQuery(id+"F27.opExtrude","CAP_EDGE",EDGE,{"disambiguationData":[OSD([sQuery(id+"F24.wireOp",EDGE,"E26.bottom")])],"isStart":true});
            var Q45;
            Q45=makeQuery(id+"F27.opExtrude","CAP_EDGE",EDGE,{"disambiguationData":[OSD([sQuery(id+"F24.wireOp",EDGE,"E26.left")])],"isStart":true});
            var Q46;
            Q46=makeQuery(id+"F27.opExtrude","CAP_EDGE",EDGE,{"disambiguationData":[OSD([sQuery(id+"F24.wireOp",EDGE,"E26.top")])],"isStart":true});
            var Q47;
            Q47=makeQuery(id+"F27.opExtrude","CAP_EDGE",EDGE,{"disambiguationData":[OSD([sQuery(id+"F24.wireOp",EDGE,"E26.right")])],"isStart":true});
            var Q48;
            Q48=makeQuery(id+"F27.opExtrude","CAP_EDGE",EDGE,{"disambiguationData":[OSD([sQuery(id+"F24.wireOp",EDGE,"E27.0.1.2")])],"isStart":true});
            var Q49;
            Q49=makeQuery(id+"F27.opExtrude","CAP_EDGE",EDGE,{"disambiguationData":[OSD([sQuery(id+"F24.wireOp",EDGE,"E27.0.1.1")])],"isStart":true});
            var Q50;
            Q50=makeQuery(id+"F27.opExtrude","CAP_EDGE",EDGE,{"disambiguationData":[OSD([sQuery(id+"F24.wireOp",EDGE,"E27.0.1.0")])],"isStart":true});
            var Q51;
            Q51=makeQuery(id+"F27.opExtrude","CAP_EDGE",EDGE,{"disambiguationData":[OSD([sQuery(id+"F24.wireOp",EDGE,"E27.0.1.3")])],"isStart":true});
            var Q52;
            Q52=makeQuery(id+"F27.opExtrude","CAP_EDGE",EDGE,{"disambiguationData":[OSD([sQuery(id+"F24.wireOp",EDGE,"E27.0.2.0")])],"isStart":true});
            var Q53;
            Q53=makeQuery(id+"F27.opExtrude","CAP_EDGE",EDGE,{"disambiguationData":[OSD([sQuery(id+"F24.wireOp",EDGE,"E27.0.2.1")])],"isStart":true});
            var Q54;
            Q54=makeQuery(id+"F27.opExtrude","CAP_EDGE",EDGE,{"disambiguationData":[OSD([sQuery(id+"F24.wireOp",EDGE,"E27.0.2.2")])],"isStart":true});
            var Q55;
            Q55=makeQuery(id+"F27.opExtrude","CAP_EDGE",EDGE,{"disambiguationData":[OSD([sQuery(id+"F24.wireOp",EDGE,"E27.0.2.3")])],"isStart":true});
            fillet(context, id + "F33", {"entities" : qUnion([Q0, Q1, Q2, Q3, Q4, Q5, Q6, Q7, Q8, Q9, Q10, Q11, Q12, Q13, Q14, Q15, Q16, Q17, Q18, Q19, Q20, Q21, Q22, Q23, Q24, Q25, Q26, Q27, Q28, Q29, Q30, Q31, Q32, Q33, Q34, Q35, Q36, Q37, Q38, Q39, Q40, Q41, Q42, Q43, Q44, Q45, Q46, Q47, Q48, Q49, Q50, Q51, Q52, Q53, Q54, Q55]), "radius" : 2 * mm, "tangentPropagation" : true, "allowEdgeOverflow" : false});
        }
        {
            var Q0;
            Q0=makeQuery(id+"F32.opExtrude","CAP_EDGE",EDGE,{"disambiguationData":[OSD([sQuery(id+"F31.wireOp",EDGE,"E32")])],"isStart":false});
            fillet(context, id + "F34", {"entities" : qUnion([Q0]), "radius" : 11.1 * mm, "tangentPropagation" : true, "allowEdgeOverflow" : false});
        }
        {
            var Q0;
            Q0=qCreatedBy(makeId("Front.planeOp"),FACE);
            var sketch = newSketch(context, id + "F35", { "sketchPlane" : qUnion([Q0])});
            skLineSegment(sketch, "E33.bottom", {"start": v(-26.89, 51.46) * mm, "end": v(-31.77, 51.46) * mm});
            skLineSegment(sketch, "E33.top", {"start": v(-26.89, 38.04) * mm, "end": v(-31.77, 38.04) * mm});
            skLineSegment(sketch, "E33.left", {"start": v(-26.89, 51.46) * mm, "end": v(-26.89, 38.04) * mm});
            skLineSegment(sketch, "E33.right", {"start": v(-31.77, 51.46) * mm, "end": v(-31.77, 38.04) * mm});
            skFitSpline(sketch, "E34", {"points": [v(-26.89, 50.72) * mm, v(-29.48, 45.2) * mm, v(-31.77, 39.8) * mm], "startDerivative": vector(0, -20.02) * mm, "endDerivative": vector(0, -14.5) * mm});
            skLineSegment(sketch, "E35.bottom", {"start": v(-26.9, 34.25) * mm, "end": v(-31.8, 34.25) * mm});
            skLineSegment(sketch, "E35.top", {"start": v(-26.9, 20.84) * mm, "end": v(-31.8, 20.84) * mm});
            skLineSegment(sketch, "E35.left", {"start": v(-26.9, 34.25) * mm, "end": v(-26.9, 20.84) * mm});
            skLineSegment(sketch, "E35.right", {"start": v(-31.8, 34.25) * mm, "end": v(-31.8, 20.84) * mm});
            skFitSpline(sketch, "E36", {"points": [v(-26.9, 33.5) * mm, v(-29.5, 28) * mm, v(-31.8, 22.6) * mm], "startDerivative": vector(0, -20.02) * mm, "endDerivative": vector(0, -14.5) * mm});
            skLineSegment(sketch, "E37.bottom", {"start": v(-26.94, 17.35) * mm, "end": v(-31.82, 17.35) * mm});
            skLineSegment(sketch, "E37.top", {"start": v(-26.94, 3.93) * mm, "end": v(-31.82, 3.93) * mm});
            skLineSegment(sketch, "E37.left", {"start": v(-26.94, 17.35) * mm, "end": v(-26.94, 3.93) * mm});
            skLineSegment(sketch, "E37.right", {"start": v(-31.82, 17.35) * mm, "end": v(-31.82, 3.93) * mm});
            skFitSpline(sketch, "E38", {"points": [v(-26.94, 16.6) * mm, v(-29.53, 11.1) * mm, v(-31.82, 5.7) * mm], "startDerivative": vector(0, -20.02) * mm, "endDerivative": vector(0, -14.5) * mm});
            skLineSegment(sketch, "E39.right", {"start": v(-63.23, 51.51) * mm, "end": v(-63.23, 38.1) * mm});
            skLineSegment(sketch, "E40.right", {"start": v(-63.25, 34.3) * mm, "end": v(-63.25, 20.88) * mm});
            skLineSegment(sketch, "E41.right", {"start": v(-63.28, 17.4) * mm, "end": v(-63.28, 3.98) * mm});
            skFitSpline(sketch, "E42.MirrorCS", {"points": [v(-68.1, 33.56) * mm, v(-65.5, 28.04) * mm, v(-63.22, 22.65) * mm], "startDerivative": vector(0, -20.02) * mm, "endDerivative": vector(0, -14.5) * mm});
            skFitSpline(sketch, "E43.MirrorCS", {"points": [v(-68.12, 50.76) * mm, v(-65.52, 45.25) * mm, v(-63.23, 39.86) * mm], "startDerivative": vector(0, -20.02) * mm, "endDerivative": vector(0, -14.5) * mm});
            skFitSpline(sketch, "E44.MirrorCS", {"points": [v(-68.07, 16.65) * mm, v(-65.48, 11.14) * mm, v(-63.18, 5.74) * mm], "startDerivative": vector(0, -20.02) * mm, "endDerivative": vector(0, -14.5) * mm});
            skLineSegment(sketch, "E45.MirrorCS", {"start": v(-68.1, 34.3) * mm, "end": v(-68.1, 20.88) * mm});
            skLineSegment(sketch, "E46.MirrorCS", {"start": v(-68.12, 51.51) * mm, "end": v(-68.12, 38.1) * mm});
            skLineSegment(sketch, "E47.MirrorCS", {"start": v(-68.07, 17.4) * mm, "end": v(-63.18, 17.4) * mm});
            skLineSegment(sketch, "E48.MirrorCS", {"start": v(-63.22, 34.3) * mm, "end": v(-63.22, 20.88) * mm});
            skLineSegment(sketch, "E49.MirrorCS", {"start": v(-68.1, 20.88) * mm, "end": v(-63.22, 20.88) * mm});
            skLineSegment(sketch, "E50.MirrorCS", {"start": v(-63.18, 17.4) * mm, "end": v(-63.18, 3.98) * mm});
            skLineSegment(sketch, "E51.MirrorCS", {"start": v(-68.12, 51.51) * mm, "end": v(-63.23, 51.51) * mm});
            skLineSegment(sketch, "E52.MirrorCS", {"start": v(-68.07, 17.4) * mm, "end": v(-68.07, 3.98) * mm});
            skLineSegment(sketch, "E53.MirrorCS", {"start": v(-68.1, 34.3) * mm, "end": v(-63.22, 34.3) * mm});
            skLineSegment(sketch, "E54.MirrorCS", {"start": v(-68.12, 38.1) * mm, "end": v(-63.23, 38.1) * mm});
            skLineSegment(sketch, "E55.MirrorCS", {"start": v(-68.07, 3.98) * mm, "end": v(-63.18, 3.98) * mm});
            skSolve(sketch);
        }
        {
            var Q0;
            {var subQ2=sQuery(id+"F35.wireOp",EDGE,"E33.top");Q0=makeQuery(id+"F35.imprint","IMPRINT",FACE,{"disambiguationData":[TD([[makeQuery(id+"F35.imprint","IMPRINT",EDGE,{"derivedFrom":subQ2}),-1.0]])]});}
            var Q1;
            {var subQ0=sQuery(id+"F35.wireOp",EDGE,"E35.top");Q1=makeQuery(id+"F35.imprint","IMPRINT",FACE,{"disambiguationData":[TD([[makeQuery(id+"F35.imprint","IMPRINT",EDGE,{"derivedFrom":subQ0}),-1.0]])]});}
            var Q2;
            {var subQ0=sQuery(id+"F35.wireOp",EDGE,"E37.top");Q2=makeQuery(id+"F35.imprint","IMPRINT",FACE,{"disambiguationData":[TD([[makeQuery(id+"F35.imprint","IMPRINT",EDGE,{"derivedFrom":subQ0}),-1.0]])]});}
            var Q3;
            {var subQ2=sQuery(id+"F35.wireOp",EDGE,"E43.MirrorCS");Q3=makeQuery(id+"F35.imprint","IMPRINT",FACE,{"disambiguationData":[TD([[makeQuery(id+"F35.imprint","IMPRINT",EDGE,{"derivedFrom":subQ2}),-1.0]])]});}
            var Q4;
            {var subQ0=sQuery(id+"F35.wireOp",EDGE,"E49.MirrorCS");var subQ1=sQuery(id+"F35.wireOp",EDGE,"E40.right");var subQ2=makeQuery(id+"F35.imprint","INTERSECT",VERTEX,{"derivedFrom":[subQ1,subQ0]});Q4=makeQuery(id+"F35.imprint","IMPRINT",FACE,{"disambiguationData":[TD([[makeQuery(id+"F35.imprint","IMPRINT",EDGE,{"disambiguationData":[TD([[subQ2,1.0]])],"derivedFrom":subQ1}),-1.0]])]});}
            var Q5;
            {var subQ0=sQuery(id+"F35.wireOp",EDGE,"E55.MirrorCS");var subQ1=sQuery(id+"F35.wireOp",EDGE,"E41.right");var subQ2=makeQuery(id+"F35.imprint","INTERSECT",VERTEX,{"derivedFrom":[subQ1,subQ0]});Q5=makeQuery(id+"F35.imprint","IMPRINT",FACE,{"disambiguationData":[TD([[makeQuery(id+"F35.imprint","IMPRINT",EDGE,{"disambiguationData":[TD([[subQ2,1.0]])],"derivedFrom":subQ1}),-1.0]])]});}
            extrude(context, id + "F36", {"entities" : qUnion([Q0, Q1, Q2, Q3, Q4, Q5]), "operationType" : NewBodyOperationType.REMOVE, "endBound" : BoundingType.THROUGH_ALL, "depth" : 25 * mm});
        }
        {
            var Q0;
            Q0=qCreatedBy(makeId("Right.planeOp"),FACE);
            var sketch = newSketch(context, id + "F37", { "sketchPlane" : qUnion([Q0])});
            skLineSegment(sketch, "E56.bottom", {"start": v(11.2, 51.43) * mm, "end": v(6.3, 51.43) * mm});
            skLineSegment(sketch, "E56.top", {"start": v(11.2, 38.01) * mm, "end": v(6.3, 38.01) * mm});
            skLineSegment(sketch, "E56.left", {"start": v(11.2, 51.43) * mm, "end": v(11.2, 38.01) * mm});
            skLineSegment(sketch, "E56.right", {"start": v(6.3, 51.43) * mm, "end": v(6.3, 38.01) * mm});
            skFitSpline(sketch, "E57", {"points": [v(11.2, 50.68) * mm, v(8.6, 45.17) * mm, v(6.3, 39.77) * mm], "startDerivative": vector(0, -20.02) * mm, "endDerivative": vector(0, -14.5) * mm});
            skLineSegment(sketch, "E58.bottom", {"start": v(11.18, 34.22) * mm, "end": v(6.3, 34.22) * mm});
            skLineSegment(sketch, "E58.top", {"start": v(11.18, 20.8) * mm, "end": v(6.3, 20.8) * mm});
            skLineSegment(sketch, "E58.left", {"start": v(11.18, 34.22) * mm, "end": v(11.18, 20.8) * mm});
            skLineSegment(sketch, "E58.right", {"start": v(6.3, 34.22) * mm, "end": v(6.3, 20.8) * mm});
            skFitSpline(sketch, "E59", {"points": [v(11.18, 33.47) * mm, v(8.58, 27.96) * mm, v(6.3, 22.56) * mm], "startDerivative": vector(0, -20.02) * mm, "endDerivative": vector(0, -14.5) * mm});
            skLineSegment(sketch, "E60.bottom", {"start": v(11.15, 17.32) * mm, "end": v(6.26, 17.32) * mm});
            skLineSegment(sketch, "E60.top", {"start": v(11.15, 3.9) * mm, "end": v(6.26, 3.9) * mm});
            skLineSegment(sketch, "E60.left", {"start": v(11.15, 17.32) * mm, "end": v(11.15, 3.9) * mm});
            skLineSegment(sketch, "E60.right", {"start": v(6.26, 17.32) * mm, "end": v(6.26, 3.9) * mm});
            skFitSpline(sketch, "E61", {"points": [v(11.15, 16.57) * mm, v(8.55, 11.06) * mm, v(6.26, 5.66) * mm], "startDerivative": vector(0, -20.02) * mm, "endDerivative": vector(0, -14.5) * mm});
            skLineSegment(sketch, "E62.right", {"start": v(-25.15, 51.48) * mm, "end": v(-25.15, 38.06) * mm});
            skLineSegment(sketch, "E63.right", {"start": v(-25.17, 34.27) * mm, "end": v(-25.17, 20.85) * mm});
            skLineSegment(sketch, "E64.right", {"start": v(-25.2, 17.36) * mm, "end": v(-25.2, 3.94) * mm});
            skFitSpline(sketch, "E65.MirrorCS", {"points": [v(-30.02, 33.52) * mm, v(-27.42, 28.01) * mm, v(-25.13, 22.61) * mm], "startDerivative": vector(0, -20.02) * mm, "endDerivative": vector(0, -14.5) * mm});
            skFitSpline(sketch, "E66.MirrorCS", {"points": [v(-30.04, 50.73) * mm, v(-27.44, 45.22) * mm, v(-25.15, 39.82) * mm], "startDerivative": vector(0, -20.02) * mm, "endDerivative": vector(0, -14.5) * mm});
            skFitSpline(sketch, "E67.MirrorCS", {"points": [v(-29.99, 16.62) * mm, v(-27.4, 11.1) * mm, v(-25.1, 5.7) * mm], "startDerivative": vector(0, -20.02) * mm, "endDerivative": vector(0, -14.5) * mm});
            skLineSegment(sketch, "E68.MirrorCS", {"start": v(-30.02, 34.27) * mm, "end": v(-30.02, 20.85) * mm});
            skLineSegment(sketch, "E69.MirrorCS", {"start": v(-30.04, 51.48) * mm, "end": v(-30.04, 38.06) * mm});
            skLineSegment(sketch, "E70.MirrorCS", {"start": v(-29.99, 17.36) * mm, "end": v(-25.1, 17.36) * mm});
            skLineSegment(sketch, "E71.MirrorCS", {"start": v(-25.13, 34.27) * mm, "end": v(-25.13, 20.85) * mm});
            skLineSegment(sketch, "E72.MirrorCS", {"start": v(-30.02, 20.85) * mm, "end": v(-25.13, 20.85) * mm});
            skLineSegment(sketch, "E73.MirrorCS", {"start": v(-25.1, 17.36) * mm, "end": v(-25.1, 3.94) * mm});
            skLineSegment(sketch, "E74.MirrorCS", {"start": v(-30.04, 51.48) * mm, "end": v(-25.15, 51.48) * mm});
            skLineSegment(sketch, "E75.MirrorCS", {"start": v(-29.99, 17.36) * mm, "end": v(-29.99, 3.94) * mm});
            skLineSegment(sketch, "E76.MirrorCS", {"start": v(-30.02, 34.27) * mm, "end": v(-25.13, 34.27) * mm});
            skLineSegment(sketch, "E77.MirrorCS", {"start": v(-30.04, 38.06) * mm, "end": v(-25.15, 38.06) * mm});
            skLineSegment(sketch, "E78.MirrorCS", {"start": v(-29.99, 3.94) * mm, "end": v(-25.1, 3.94) * mm});
            skSolve(sketch);
        }
        {
            var Q0;
            {var subQ0=sQuery(id+"F37.wireOp",EDGE,"E78.MirrorCS");var subQ1=sQuery(id+"F37.wireOp",EDGE,"E64.right");var subQ2=makeQuery(id+"F37.imprint","INTERSECT",VERTEX,{"derivedFrom":[subQ1,subQ0]});Q0=makeQuery(id+"F37.imprint","IMPRINT",FACE,{"disambiguationData":[TD([[makeQuery(id+"F37.imprint","IMPRINT",EDGE,{"disambiguationData":[TD([[subQ2,1.0]])],"derivedFrom":subQ1}),-1.0]])]});}
            var Q1;
            {var subQ0=sQuery(id+"F37.wireOp",EDGE,"E72.MirrorCS");var subQ1=sQuery(id+"F37.wireOp",EDGE,"E63.right");var subQ2=makeQuery(id+"F37.imprint","INTERSECT",VERTEX,{"derivedFrom":[subQ1,subQ0]});Q1=makeQuery(id+"F37.imprint","IMPRINT",FACE,{"disambiguationData":[TD([[makeQuery(id+"F37.imprint","IMPRINT",EDGE,{"disambiguationData":[TD([[subQ2,1.0]])],"derivedFrom":subQ1}),-1.0]])]});}
            var Q2;
            {var subQ2=sQuery(id+"F37.wireOp",EDGE,"E66.MirrorCS");Q2=makeQuery(id+"F37.imprint","IMPRINT",FACE,{"disambiguationData":[TD([[makeQuery(id+"F37.imprint","IMPRINT",EDGE,{"derivedFrom":subQ2}),-1.0]])]});}
            var Q3;
            {var subQ0=sQuery(id+"F37.wireOp",EDGE,"E56.top");Q3=makeQuery(id+"F37.imprint","IMPRINT",FACE,{"disambiguationData":[TD([[makeQuery(id+"F37.imprint","IMPRINT",EDGE,{"derivedFrom":subQ0}),-1.0]])]});}
            var Q4;
            {var subQ0=sQuery(id+"F37.wireOp",EDGE,"E58.top");Q4=makeQuery(id+"F37.imprint","IMPRINT",FACE,{"disambiguationData":[TD([[makeQuery(id+"F37.imprint","IMPRINT",EDGE,{"derivedFrom":subQ0}),-1.0]])]});}
            var Q5;
            {var subQ0=sQuery(id+"F37.wireOp",EDGE,"E60.top");Q5=makeQuery(id+"F37.imprint","IMPRINT",FACE,{"disambiguationData":[TD([[makeQuery(id+"F37.imprint","IMPRINT",EDGE,{"derivedFrom":subQ0}),-1.0]])]});}
            extrude(context, id + "F38", {"entities" : qUnion([Q0, Q1, Q2, Q3, Q4, Q5]), "operationType" : NewBodyOperationType.REMOVE, "endBound" : BoundingType.THROUGH_ALL, "oppositeDirection" : true, "depth" : 25 * mm});
        }
        {
            var Q0;
            Q0=makeQuery(id+"F1.opExtrude","SWEPT_FACE",FACE,{"disambiguationData":[OSD([sQuery(id+"F0.wireOp",EDGE,"E0.bottom")])]});
            var sketch = newSketch(context, id + "F39", { "sketchPlane" : qUnion([Q0])});
            skCircle(sketch, "E79", {"center": v(-13.07, -9.5) * mm, "radius": 7 * mm});
            skSolve(sketch);
        }
        {
            var Q0;
            Q0=makeQuery(id+"F39.imprint","IMPRINT",FACE,{"disambiguationData":[TD([[makeQuery(id+"F39.imprint","IMPRINT",EDGE,{"derivedFrom":sQuery(id+"F39.wireOp",EDGE,"E79")}),1.0]])]});
            extrude(context, id + "F40", {"entities" : qUnion([Q0]), "operationType" : NewBodyOperationType.REMOVE, "endBound" : BoundingType.THROUGH_ALL, "oppositeDirection" : true, "depth" : 25 * mm});
        }
    });
